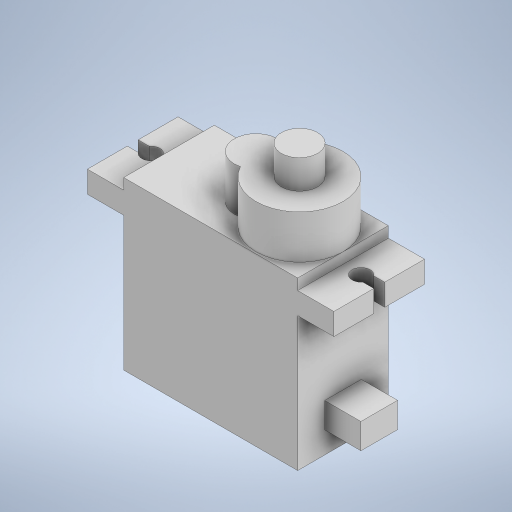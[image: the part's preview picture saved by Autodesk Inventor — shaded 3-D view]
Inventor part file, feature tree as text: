
AUTODESK INVENTOR PART (.ipt)
format: ipt  version: 2023 (Build 270158000, 158)  size: 340,480 bytes
history: native  units: in
note: dims shown in document units (in); Inventor stores cm internally (conversion verified against a paired STEP export)
features: sketch x7, projected_geometry x7, extrude x6
ambient origin geometry x8: Origin, YZ Plane, XZ Plane, XY Plane, X Axis, Y Axis, Z Axis, Center Point
bodies: Solid1 (feature_tree)
feature tree (20):
  extrude  "Extrusion1"  Depth=0.1575in
  extrude  "Extrusion2"  Depth=0.2362in
  extrude  "Extrusion3"  Depth=1.3386in
  extrude  "Extrusion4"  Depth=0.0591in
  extrude  "Extrusion5"  Depth=0.4921in TaperAngle=0.0deg
  sketch  "草圖7"
  extrude  "Extrusion6"  Depth=0.2362in TaperAngle=0.0deg
  sketch  "Sketch1"  dims[d0=0.1969in d1=0.1575in]
  sketch  "Sketch2"  dims[d2=0.2362in d3=0.2362in]
  sketch  "Sketch3"  dims[d4=0.9449in d6=1.3386in]
  sketch  "Sketch4"  dims[d7=0.3543in d8=0.0591in]
  sketch  "Sketch5"  dims[d9=0.1181in d10=0.4921in d11=0.0in]
  projected_geometry  "Projected Loop1"
  projected_geometry  "Projected Loop2"
  sketch  "Sketch6"  dims[d12=0.3543in d13=0.2362in d14=0.0in d15=0.1969in d16=0.1575in d17=0.0in d18=0.1181in d19=0.4724in d20=0.1969in d21=0.0in d22=0.0984in d23=1.1417in d24=0.0591in d25=0.0591in d26=0.1181in d27=0.0in d28=0.7874in d29=0.1378in d30=0.0in d31=0.7283in]
  projected_geometry  "投影迴路3"
  projected_geometry  "投影迴路4"
  projected_geometry  "投影迴路5"
  projected_geometry  "投影迴路6"
  projected_geometry  "投影迴路7"
